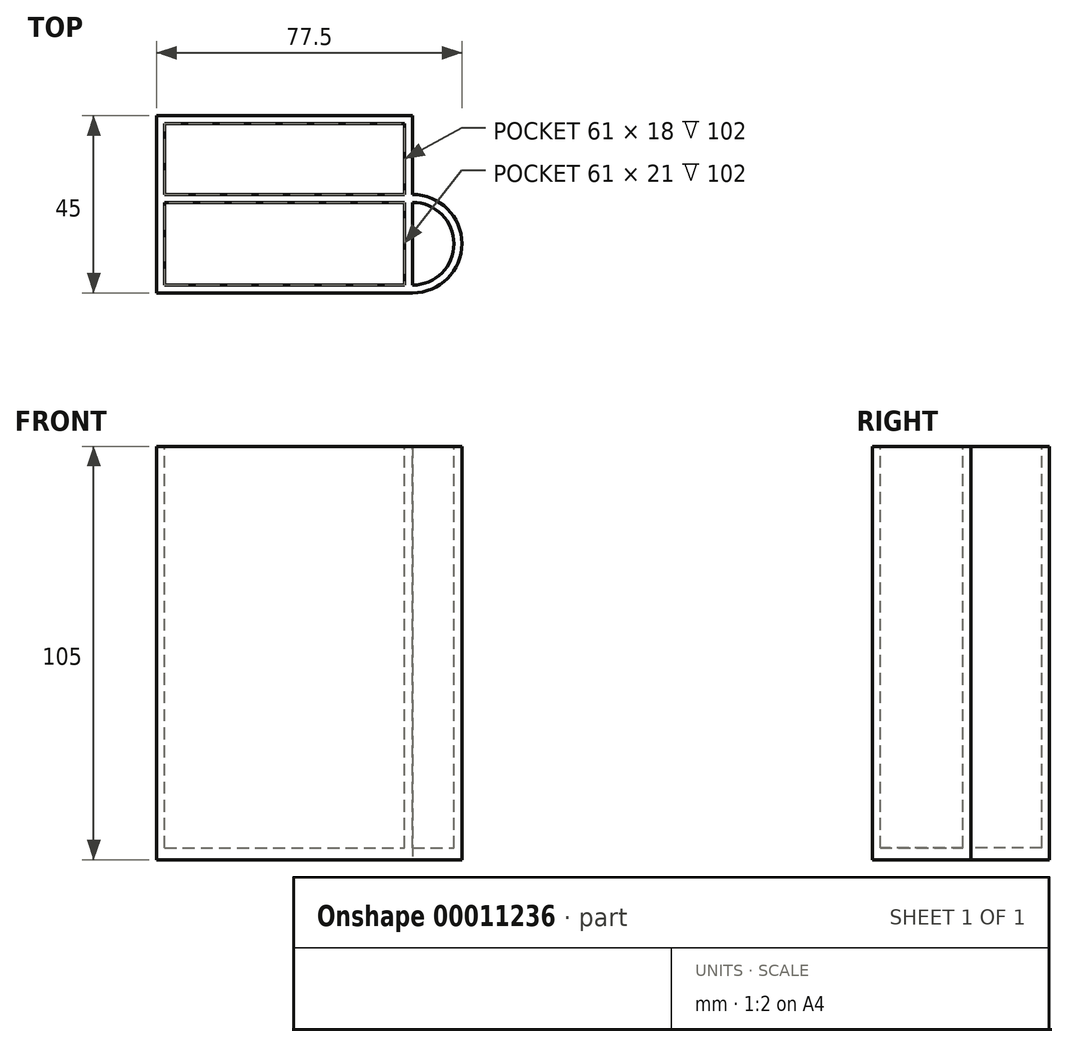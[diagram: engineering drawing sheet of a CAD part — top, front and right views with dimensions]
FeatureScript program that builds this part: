
annotation { "Feature Type Name" : "Feature", "Feature Type Description" : "" }
export const myFeature = defineFeature(function(context is Context, id is Id, definition is map)
    precondition{}
    {
        {
            var Q0;
            Q0=qCreatedBy(makeId("Top.planeOp"),FACE);
            var sketch = newSketch(context, id + "F0", { "sketchPlane" : qUnion([Q0])});
            skLineSegment(sketch, "E0.bottom", {"start": v(0, 0) * mm, "end": v(65, 0) * mm});
            skLineSegment(sketch, "E0.top", {"start": v(0, 45) * mm, "end": v(65, 45) * mm});
            skLineSegment(sketch, "E0.left", {"start": v(0, 0) * mm, "end": v(0, 45) * mm});
            skArc(sketch, "E1", {"start": v(65, 0) * mm, "mid": v(77.5, 12.5) * mm, "end": v(65, 25) * mm});
            skLineSegment(sketch, "E2.trimOffspring", {"start": v(65, 25) * mm, "end": v(65, 45) * mm});
            skSolve(sketch);
        }
        {
            var Q0;
            Q0=makeQuery(id+"F0.imprint","IMPRINT",FACE,{"disambiguationData":[TD([[makeQuery(id+"F0.imprint","IMPRINT",EDGE,{"derivedFrom":sQuery(id+"F0.wireOp",EDGE,"E0.bottom")}),1.0]])]});
            extrude(context, id + "F1", {"entities" : qUnion([Q0]), "depth" : 105 * mm});
        }
        {
            var Q0;
            Q0=makeQuery(id+"F1.opExtrude","CAP_FACE",FACE,{"disambiguationData":[OSD([sQuery(id+"F0.wireOp",EDGE,"E0.bottom"),sQuery(id+"F0.wireOp",EDGE,"E0.top"),sQuery(id+"F0.wireOp",EDGE,"E0.left"),sQuery(id+"F0.wireOp",EDGE,"E1"),sQuery(id+"F0.wireOp",EDGE,"E2.trimOffspring")])],"isStart":false});
            var sketch = newSketch(context, id + "F2", { "sketchPlane" : qUnion([Q0])});
            skLineSegment(sketch, "E3.0", {"start": v(2, 43) * mm, "end": v(2, 2) * mm});
            skLineSegment(sketch, "E3.1", {"start": v(63, 43) * mm, "end": v(2, 43) * mm});
            skLineSegment(sketch, "E3.4", {"start": v(2, 2) * mm, "end": v(63, 2) * mm});
            skLineSegment(sketch, "E4", {"start": v(63, 43) * mm, "end": v(63, 2) * mm});
            skArc(sketch, "E5.0", {"start": v(65, 2) * mm, "mid": v(75.5, 12.5) * mm, "end": v(65, 23) * mm});
            skLineSegment(sketch, "E6", {"start": v(65, 23) * mm, "end": v(65, 2) * mm});
            skSolve(sketch);
        }
        {
            var Q0;
            Q0 = qSketchRegion(id + "F2", true);
            extrude(context, id + "F3", {"entities" : qUnion([Q0]), "operationType" : NewBodyOperationType.REMOVE, "oppositeDirection" : true, "depth" : 102 * mm});
        }
        {
            var Q0;
            Q0=makeQuery(id+"F1.opExtrude","CAP_FACE",FACE,{"disambiguationData":[OSD([sQuery(id+"F0.wireOp",EDGE,"E0.bottom"),sQuery(id+"F0.wireOp",EDGE,"E0.top"),sQuery(id+"F0.wireOp",EDGE,"E0.left"),sQuery(id+"F0.wireOp",EDGE,"E1"),sQuery(id+"F0.wireOp",EDGE,"E2.trimOffspring")])],"isStart":false});
            var sketch = newSketch(context, id + "F4", { "sketchPlane" : qUnion([Q0])});
            skLineSegment(sketch, "E7", {"start": v(63, 25) * mm, "end": v(2, 25) * mm});
            skLineSegment(sketch, "E8", {"start": v(2, 25) * mm, "end": v(2, 23) * mm});
            skLineSegment(sketch, "E9", {"start": v(2, 23) * mm, "end": v(63, 23) * mm});
            skLineSegment(sketch, "E10", {"start": v(63, 23) * mm, "end": v(63, 25) * mm});
            skSolve(sketch);
        }
        {
            var Q0;
            Q0=makeQuery(id+"F4.imprint","IMPRINT",FACE,{"disambiguationData":[TD([[makeQuery(id+"F4.imprint","IMPRINT",EDGE,{"derivedFrom":sQuery(id+"F4.wireOp",EDGE,"E7")}),1.0]])]});
            extrude(context, id + "F5", {"entities" : qUnion([Q0]), "operationType" : NewBodyOperationType.ADD, "endBound" : BoundingType.UP_TO_NEXT, "oppositeDirection" : true, "depth" : 25 * mm});
        }
    });
